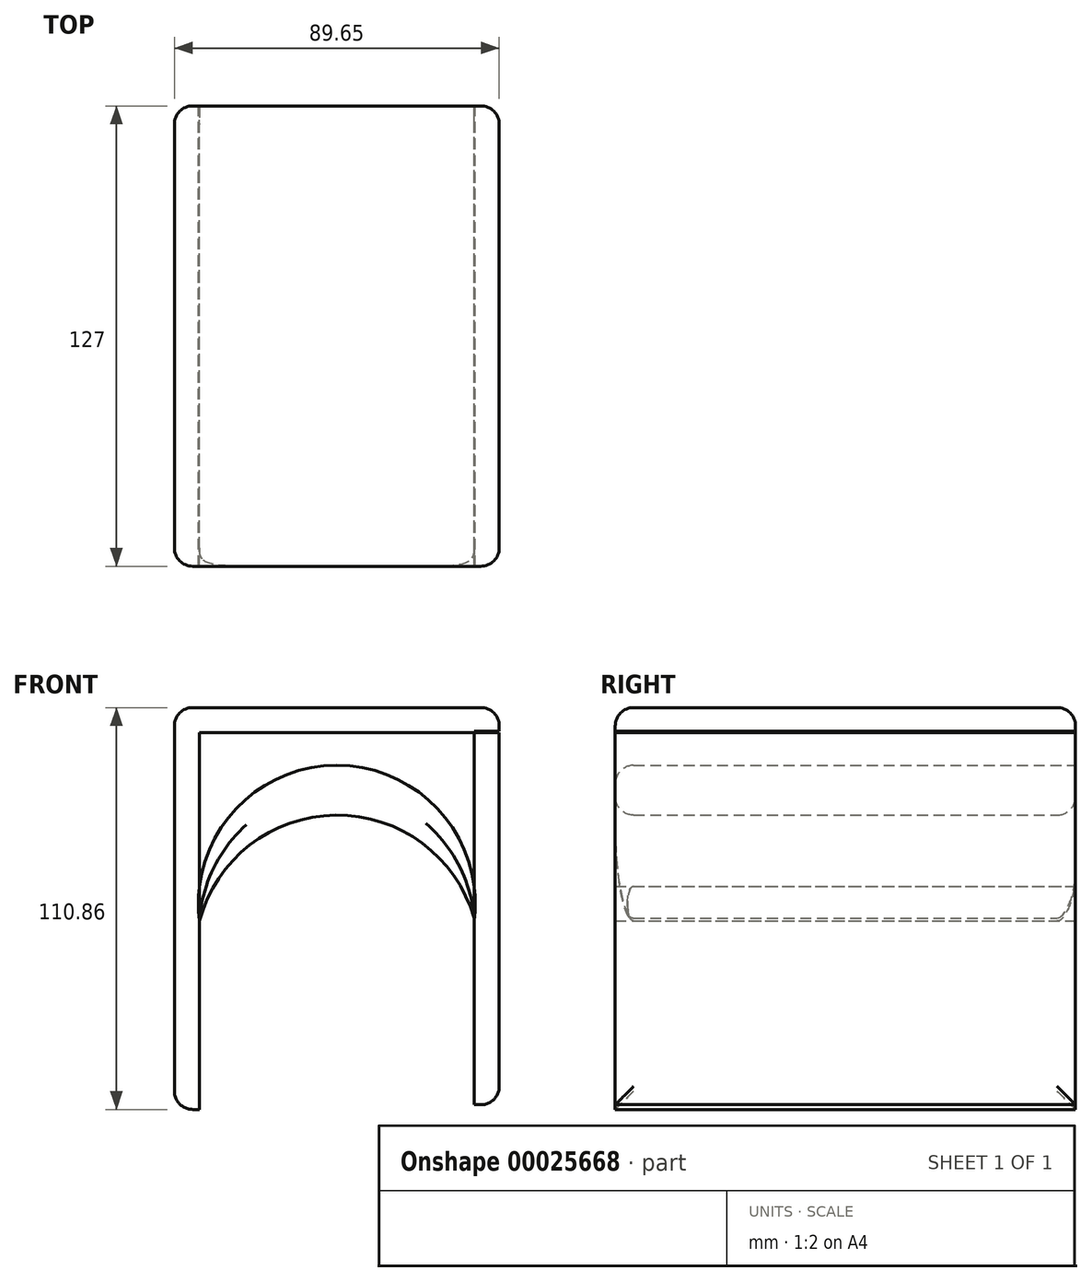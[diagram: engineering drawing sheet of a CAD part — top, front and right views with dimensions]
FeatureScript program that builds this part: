
annotation { "Feature Type Name" : "Feature", "Feature Type Description" : "" }
export const myFeature = defineFeature(function(context is Context, id is Id, definition is map)
    precondition{}
    {
        {
            var Q0;
            Q0=qCreatedBy(makeId("Front.planeOp"),FACE);
            var sketch = newSketch(context, id + "F0", { "sketchPlane" : qUnion([Q0])});
            skLineSegment(sketch, "E0.bottom", {"start": v(35.08, 30.31) * mm, "end": v(42, 30.31) * mm});
            skLineSegment(sketch, "E0.top", {"start": v(35.08, -72.76) * mm, "end": v(42, -72.76) * mm});
            skLineSegment(sketch, "E0.left", {"start": v(35.08, 30.31) * mm, "end": v(35.08, -72.76) * mm});
            skLineSegment(sketch, "E0.right", {"start": v(42, 30.31) * mm, "end": v(42, -72.76) * mm});
            skLineSegment(sketch, "E1.bottom", {"start": v(-47.64, 29.88) * mm, "end": v(-40.7, 29.88) * mm});
            skLineSegment(sketch, "E1.top", {"start": v(-47.64, -74.05) * mm, "end": v(-40.7, -74.05) * mm});
            skLineSegment(sketch, "E1.left", {"start": v(-47.64, 29.88) * mm, "end": v(-47.64, -74.05) * mm});
            skLineSegment(sketch, "E1.right", {"start": v(-40.7, 29.88) * mm, "end": v(-40.7, -74.05) * mm});
            skPoint(sketch, "E2.2.internal.orphan", {"position": v(0, 36.81) * mm});
            skPoint(sketch, "E2.start.orphan", {"position": v(-40.7, 0) * mm});
            skPoint(sketch, "E3.1.internal.orphan", {"position": v(-24.68, 0) * mm});
            skPoint(sketch, "E3.2.internal.orphan", {"position": v(0, 20.79) * mm});
            skPoint(sketch, "E3.3.internal.orphan", {"position": v(19.92, 0) * mm});
            skArc(sketch, "E4", {"start": v(35.08, -21.22) * mm, "mid": v(-3.14, 7.15) * mm, "end": v(-40.7, -22.09) * mm});
            skArc(sketch, "E5", {"start": v(35.08, -22.09) * mm, "mid": v(-2.81, 20.9) * mm, "end": v(-40.7, -22.09) * mm});
            skLineSegment(sketch, "E6.bottom", {"start": v(-47.64, 29.88) * mm, "end": v(42, 29.88) * mm});
            skLineSegment(sketch, "E6.top", {"start": v(-47.64, 36.81) * mm, "end": v(42, 36.81) * mm});
            skLineSegment(sketch, "E6.left", {"start": v(-47.64, 29.88) * mm, "end": v(-47.64, 36.81) * mm});
            skLineSegment(sketch, "E6.right", {"start": v(42, 29.88) * mm, "end": v(42, 36.81) * mm});
            skSolve(sketch);
        }
        {
            var Q0;
            {var subQ5=sQuery(id+"F0.wireOp",EDGE,"E4");Q0=makeQuery(id+"F0.imprint","IMPRINT",FACE,{"disambiguationData":[TD([[makeQuery(id+"F0.imprint","IMPRINT",EDGE,{"derivedFrom":subQ5}),-1.0]])]});}
            var Q1;
            {var subQ5=sQuery(id+"F0.wireOp",EDGE,"E0.top");Q1=makeQuery(id+"F0.imprint","IMPRINT",FACE,{"disambiguationData":[TD([[makeQuery(id+"F0.imprint","IMPRINT",EDGE,{"derivedFrom":subQ5}),1.0]])]});}
            var Q2;
            {var subQ2=sQuery(id+"F0.wireOp",EDGE,"E0.bottom");Q2=makeQuery(id+"F0.imprint","IMPRINT",FACE,{"disambiguationData":[TD([[makeQuery(id+"F0.imprint","IMPRINT",EDGE,{"derivedFrom":subQ2}),1.0]])]});}
            var Q3;
            {var subQ3=sQuery(id+"F0.wireOp",EDGE,"E1.top");Q3=makeQuery(id+"F0.imprint","IMPRINT",FACE,{"disambiguationData":[TD([[makeQuery(id+"F0.imprint","IMPRINT",EDGE,{"derivedFrom":subQ3}),1.0]])]});}
            extrude(context, id + "F1", {"entities" : qUnion([Q0, Q1, Q2, Q3]), "depth" : 127 * mm});
        }
        {
            var Q0;
            Q0=qCreatedBy(makeId("Top.planeOp"),FACE);
            var sketch = newSketch(context, id + "F2", { "sketchPlane" : qUnion([Q0])});
            skLineSegment(sketch, "E7.bottom", {"start": v(-46.85, 0) * mm, "end": v(42.2, 0) * mm});
            skLineSegment(sketch, "E7.top", {"start": v(-46.85, -13.37) * mm, "end": v(42.2, -13.37) * mm});
            skLineSegment(sketch, "E7.left", {"start": v(-46.85, 0) * mm, "end": v(-46.85, -13.37) * mm});
            skLineSegment(sketch, "E7.right", {"start": v(42.2, 0) * mm, "end": v(42.2, -13.37) * mm});
            skSolve(sketch);
        }
        {
            var Q0;
            Q0=sQuery(id+"F2.wireOp",EDGE,"E7.right");
            var Q1;
            Q1=sQuery(id+"F2.wireOp",EDGE,"E7.top");
            var Q2;
            Q2=sQuery(id+"F2.wireOp",EDGE,"E7.left");
            var Q3;
            Q3=sQuery(id+"F2.wireOp",EDGE,"E7.bottom");
            extrude(context, id + "F3", {"bodyType" : ToolBodyType.SURFACE, "surfaceEntities" : qUnion([Q0, Q1, Q2, Q3]), "depth" : 177.8 * mm});
        }
        {
            var Q0;
            Q0=makeQuery(id+"F3.opExtrude","SWEPT_EDGE",EDGE,{"disambiguationData":[OSD([sQuery(id+"F2.wireOp",VERTEX,"E7.left.end")])]});
            var Q1;
            Q1=makeQuery(id+"F1.opExtrude","SWEPT_EDGE",EDGE,{"disambiguationData":[OSD([sQuery(id+"F0.wireOp",EDGE,"E6.top"),sQuery(id+"F0.wireOp",EDGE,"E6.left")])]});
            var Q2;
            Q2=makeQuery(id+"F1.opExtrude","SWEPT_FACE",FACE,{"disambiguationData":[OSD([sQuery(id+"F0.wireOp",EDGE,"E1.left"),sQuery(id+"F0.wireOp",EDGE,"E6.left")])]});
            var Q3;
            Q3=makeQuery(id+"F1.opExtrude","SWEPT_EDGE",EDGE,{"disambiguationData":[OSD([sQuery(id+"F0.wireOp",EDGE,"E6.top"),sQuery(id+"F0.wireOp",EDGE,"E6.right")])]});
            var Q4;
            Q4=makeQuery(id+"F3.opExtrude","SWEPT_EDGE",EDGE,{"disambiguationData":[OSD([sQuery(id+"F2.wireOp",VERTEX,"E7.bottom.end")])]});
            var Q5;
            Q5=makeQuery(id+"F3.opExtrude","SWEPT_FACE",FACE,{"disambiguationData":[OSD([sQuery(id+"F2.wireOp",EDGE,"E7.bottom")])]});
            fillet(context, id + "F4", {"entities" : qUnion([Q0, Q1, Q2, Q3, Q4, Q5]), "radius" : 5.08 * mm, "tangentPropagation" : true, "allowEdgeOverflow" : false});
        }
        {
            var Q0;
            Q0=makeQuery(id+"F1.opExtrude","CAP_EDGE",EDGE,{"disambiguationData":[OSD([sQuery(id+"F0.wireOp",EDGE,"E0.right")])],"isStart":false});
            var Q1;
            Q1=makeQuery(id+"F1.opExtrude","SWEPT_EDGE",EDGE,{"disambiguationData":[OSD([sQuery(id+"F0.wireOp",EDGE,"E0.top"),sQuery(id+"F0.wireOp",EDGE,"E0.right")])]});
            var Q2;
            Q2=makeQuery(id+"F1.opExtrude","CAP_EDGE",EDGE,{"disambiguationData":[OSD([sQuery(id+"F0.wireOp",EDGE,"E0.right")])],"isStart":true});
            var Q3;
            Q3=makeQuery(id+"F1.opExtrude","CAP_EDGE",EDGE,{"disambiguationData":[OSD([sQuery(id+"F0.wireOp",EDGE,"E4")])],"isStart":false});
            var Q4;
            {var subQ0=sQuery(id+"F0.wireOp",EDGE,"E5");Q4=makeQuery(id+"F1.opExtrude","CAP_EDGE",EDGE,{"disambiguationData":[OSD([subQ0]),TDD([makeQuery(id+"F0.imprint","IMPRINT",EDGE,{"disambiguationData":[TD([[makeQuery(id+"F0.imprint","INTERSECT",VERTEX,{"disambiguationData":[OD(1.0)],"derivedFrom":[sQuery(id+"F0.wireOp",EDGE,"E0.left"),subQ0]}),-1.0]])],"derivedFrom":subQ0})])],"isStart":false});}
            var Q5;
            Q5=makeQuery(id+"F1.opExtrude","CAP_EDGE",EDGE,{"disambiguationData":[OSD([sQuery(id+"F0.wireOp",EDGE,"E4")])],"isStart":true});
            var Q6;
            Q6=makeQuery(id+"F3.opExtrude","SWEPT_FACE",FACE,{"disambiguationData":[OSD([sQuery(id+"F2.wireOp",EDGE,"E7.bottom")])]});
            fillet(context, id + "F5", {"entities" : qUnion([Q0, Q1, Q2, Q3, Q4, Q5, Q6]), "radius" : 5.08 * mm, "tangentPropagation" : true, "allowEdgeOverflow" : false});
        }
        {
            var Q0;
            Q0=makeQuery(id+"F1.opExtrude","SWEPT_FACE",FACE,{"disambiguationData":[OSD([sQuery(id+"F0.wireOp",EDGE,"E6.top")])]});
            var Q1;
            Q1=makeQuery(id+"F1.opExtrude","CAP_EDGE",EDGE,{"disambiguationData":[OSD([sQuery(id+"F0.wireOp",EDGE,"E6.top")])],"isStart":false});
            fillet(context, id + "F6", {"entities" : qUnion([Q0, Q1]), "radius" : 5.08 * mm, "tangentPropagation" : true, "allowEdgeOverflow" : false});
        }
    });
